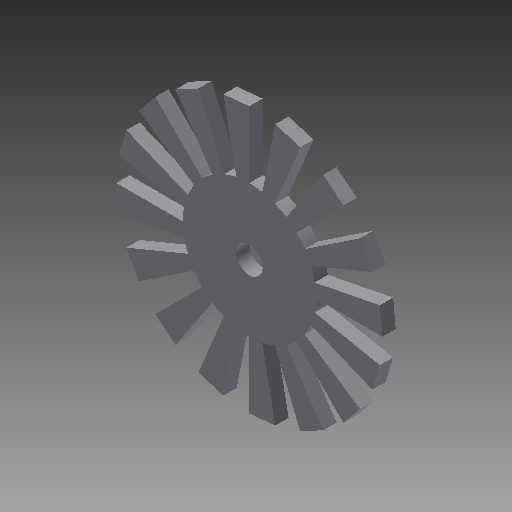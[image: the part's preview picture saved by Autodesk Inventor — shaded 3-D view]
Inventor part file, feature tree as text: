
AUTODESK INVENTOR PART (.ipt)
format: ipt  version: 2017 (Build 210142000, 142)  size: 217,088 bytes
history: native  units: mm
features: extrude x1, sketch x1
ambient origin geometry x8: Origin, YZ Plane, XZ Plane, XY Plane, X Axis, Y Axis, Z Axis, Center Point
bodies: Body1 (feature_tree)
feature tree (2):
  extrude  "Extrusion2"  Depth=1.0mm TaperAngle=0.0deg
  sketch  "Sketch1"  dims[d1=2.0mm d5=1.0mm d6=0.0mm]
